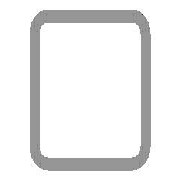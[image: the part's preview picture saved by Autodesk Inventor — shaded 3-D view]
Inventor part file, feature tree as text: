
AUTODESK INVENTOR PART (.ipt)
format: ipt  version: 2025 (Build 290162010, 162A)  size: 130,560 bytes
history: native  units: mm (DEFAULTED — no unit token found)
features: other x3, sketch x1, plane x1
ambient origin geometry x8: Origin, YZ Plane, XZ Plane, XY Plane, X Axis, Y Axis, Z Axis, Center Point
bodies: Solid1 (feature_tree), Body (feature_tree)
feature tree (5):
  other  "Driven Length"
  other  "Start plane"
  other  "End plane"
  sketch  "Sketch3"  dims[d3=140.0mm d4=0.0mm d7=4.0mm d9=40.0mm d11=40.0mm d12=2.0mm d13=-0.0mm d14=140.0mm d15=20.0mm d16=20.0mm d17=90.0deg d18=140.0mm]
  plane  "Work Plane3"
